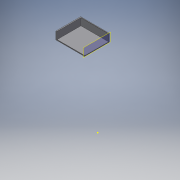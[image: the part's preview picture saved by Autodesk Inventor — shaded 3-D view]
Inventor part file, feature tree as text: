
AUTODESK INVENTOR PART (.ipt)
format: ipt  version: 2016 SP2 (Build 200236200, 236)  size: 110,592 bytes
history: native  units: mm
features: reference x7, extrude x2, sketch x2, plane x1
ambient origin geometry x8: Origin, YZ Plane, XZ Plane, XY Plane, X Axis, Y Axis, Z Axis, Center Point
bodies: Volumenkörper1 (feature_tree)
feature tree (12):
  plane  "Arbeitsebene1"
  extrude  "Extrusion1"  Depth=92.5mm TaperAngle=0.0deg
  extrude  "Extrusion2"  [1 undecoded]
  sketch  "Skizze1"  dims[d0=2.0mm d1=92.5mm d2=0.0mm]
  reference  "Referenz1"
  reference  "Referenz2"
  reference  "Referenz3"
  reference  "Referenz4"
  reference  "Referenz5"
  reference  "Referenz6"
  reference  "Referenz7"
  sketch  "Skizze3"  dims[d3=3.0mm d4=0.0mm]
note: 1 required parameter value undecoded (feature->parameter linkage not recoverable at this tier; creation-order binding heuristic only, values carry confidence <= 0.55)
